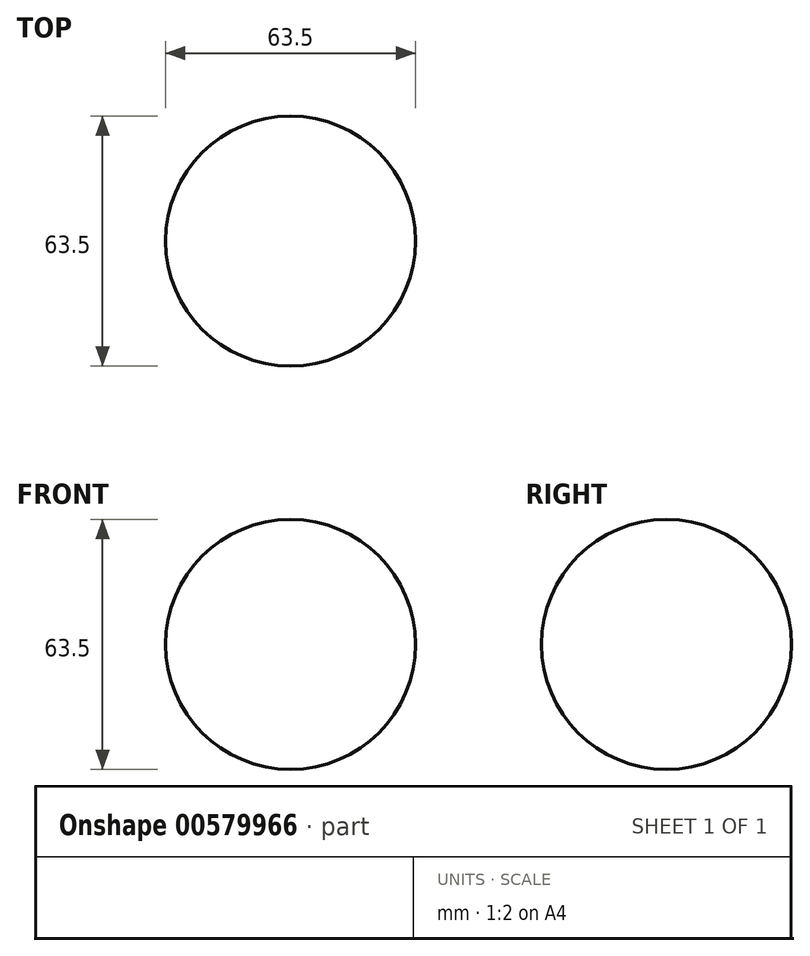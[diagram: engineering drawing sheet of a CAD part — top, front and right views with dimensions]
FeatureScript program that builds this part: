
annotation { "Feature Type Name" : "Feature", "Feature Type Description" : "" }
export const myFeature = defineFeature(function(context is Context, id is Id, definition is map)
    precondition{}
    {
        {
            var Q0;
            Q0=qCreatedBy(makeId("Front.planeOp"),FACE);
            var sketch = newSketch(context, id + "F0", { "sketchPlane" : qUnion([Q0])});
            skLineSegment(sketch, "E0", {"start": v(0, 0) * mm, "end": v(-63.5, 0) * mm});
            skCircle(sketch, "E1", {"center": v(-31.75, 0) * mm, "radius": 31.75 * mm});
            skSolve(sketch);
        }
        {
            var Q0;
            {var subQ0=sQuery(id+"F0.wireOp",EDGE,"E0");Q0=makeQuery(id+"F0.imprint","IMPRINT",FACE,{"disambiguationData":[TD([[makeQuery(id+"F0.imprint","IMPRINT",EDGE,{"derivedFrom":subQ0}),-1.0]])]});}
            var Q1;
            Q1=sQuery(id+"F0.wireOp",EDGE,"E0");
            revolve(context, id + "F1", {"entities" : qUnion([Q0]), "axis" : qUnion([Q1]), "revolveType" : RevolveType.FULL});
        }
    });
